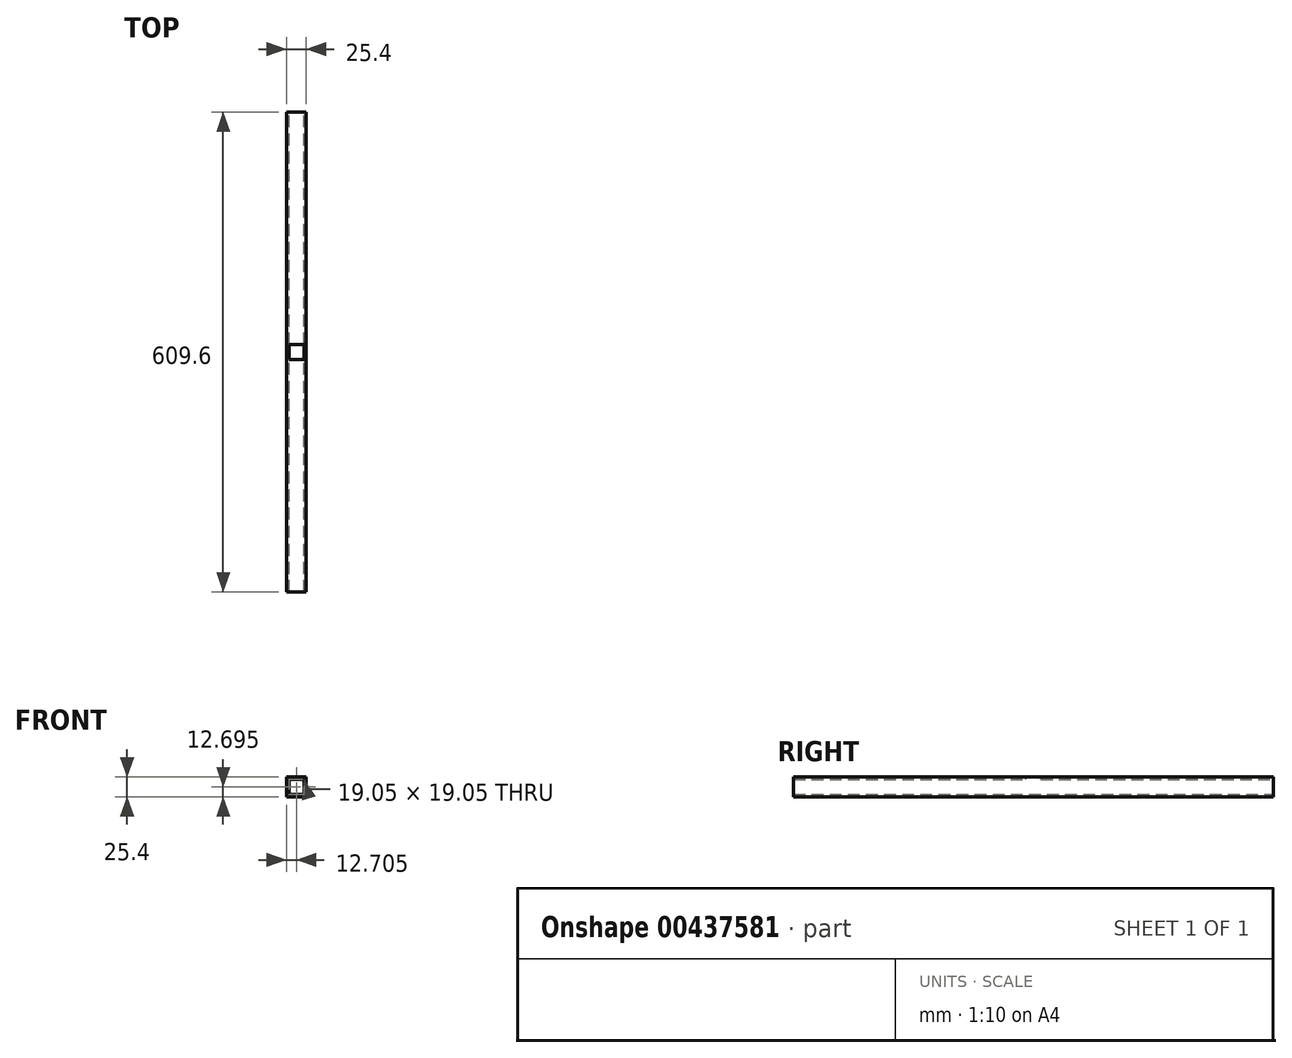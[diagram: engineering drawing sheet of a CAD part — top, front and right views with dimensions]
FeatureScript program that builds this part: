
annotation { "Feature Type Name" : "Feature", "Feature Type Description" : "" }
export const myFeature = defineFeature(function(context is Context, id is Id, definition is map)
    precondition{}
    {
        {
            var Q0;
            Q0=qCreatedBy(makeId("Front.planeOp"),FACE);
            var sketch = newSketch(context, id + "F0", { "sketchPlane" : qUnion([Q0])});
            skLineSegment(sketch, "E0.bottom", {"start": v(-22.23, 22.23) * mm, "end": v(3.17, 22.23) * mm});
            skLineSegment(sketch, "E0.top", {"start": v(-22.23, -3.18) * mm, "end": v(3.18, -3.18) * mm});
            skLineSegment(sketch, "E0.left", {"start": v(-22.23, 22.23) * mm, "end": v(-22.23, -3.18) * mm});
            skLineSegment(sketch, "E0.right", {"start": v(3.17, 22.23) * mm, "end": v(3.18, -3.18) * mm});
            skLineSegment(sketch, "E1.bottom", {"start": v(-19.05, 19.05) * mm, "end": v(0, 19.05) * mm});
            skLineSegment(sketch, "E1.top", {"start": v(-19.05, 0) * mm, "end": v(0, 0) * mm});
            skLineSegment(sketch, "E1.left", {"start": v(-19.05, 19.05) * mm, "end": v(-19.05, 0) * mm});
            skLineSegment(sketch, "E1.right", {"start": v(0, 19.05) * mm, "end": v(0, 0) * mm});
            skSolve(sketch);
        }
        {
            var Q0;
            Q0=qSketchRegion(id+"F0",true);
            extrude(context, id + "F1", {"entities" : qUnion([Q0]), "depth" : 609.6 * mm});
        }
        {
            var Q0;
            Q0=makeQuery(id+"F1.opExtrude","SWEPT_FACE",FACE,{"disambiguationData":[OSD([sQuery(id+"F0.wireOp",EDGE,"E0.bottom")])]});
            var sketch = newSketch(context, id + "F2", { "sketchPlane" : qUnion([Q0])});
            skLineSegment(sketch, "E2.bottom", {"start": v(-19.05, -295.28) * mm, "end": v(0, -295.28) * mm});
            skLineSegment(sketch, "E2.top", {"start": v(-19.05, -314.33) * mm, "end": v(0, -314.33) * mm});
            skLineSegment(sketch, "E2.left", {"start": v(-19.05, -295.28) * mm, "end": v(-19.05, -314.33) * mm});
            skLineSegment(sketch, "E2.right", {"start": v(0, -295.28) * mm, "end": v(0, -314.33) * mm});
            skSolve(sketch);
        }
        {
            var Q0;
            Q0=makeQuery(id+"F2.imprint","IMPRINT",FACE,{"disambiguationData":[TD([[makeQuery(id+"F2.imprint","IMPRINT",EDGE,{"derivedFrom":sQuery(id+"F2.wireOp",EDGE,"E2.bottom")}),-1.0]])]});
            extrude(context, id + "F3", {"entities" : qUnion([Q0]), "operationType" : NewBodyOperationType.REMOVE, "oppositeDirection" : true, "depth" : 19.05 * mm});
        }
    });
